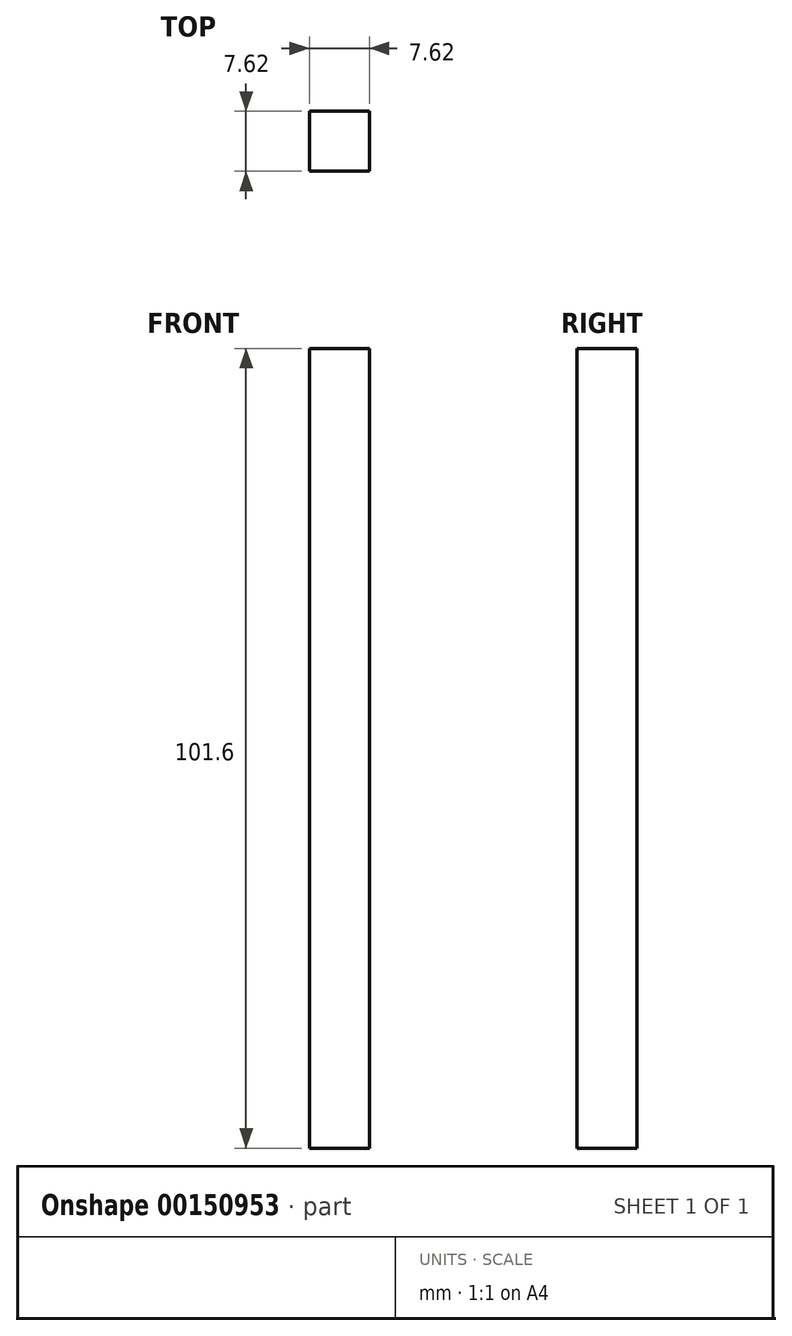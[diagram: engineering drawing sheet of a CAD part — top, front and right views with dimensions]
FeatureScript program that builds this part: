
annotation { "Feature Type Name" : "Feature", "Feature Type Description" : "" }
export const myFeature = defineFeature(function(context is Context, id is Id, definition is map)
    precondition{}
    {
        {
            var Q0;
            Q0=qCreatedBy(makeId("Front.planeOp"),FACE);
            var sketch = newSketch(context, id + "F0", { "sketchPlane" : qUnion([Q0])});
            skLineSegment(sketch, "E0.bottom", {"start": v(0, 0) * mm, "end": v(7.62, 0) * mm});
            skLineSegment(sketch, "E0.top", {"start": v(0, 101.6) * mm, "end": v(7.62, 101.6) * mm});
            skLineSegment(sketch, "E0.left", {"start": v(0, 0) * mm, "end": v(0, 101.6) * mm});
            skLineSegment(sketch, "E0.right", {"start": v(7.62, 0) * mm, "end": v(7.62, 101.6) * mm});
            skSolve(sketch);
        }
        {
            var Q0;
            Q0=makeQuery(id+"F0.imprint","IMPRINT",FACE,{"disambiguationData":[TD([[makeQuery(id+"F0.imprint","IMPRINT",EDGE,{"derivedFrom":sQuery(id+"F0.wireOp",EDGE,"E0.bottom")}),1.0]])]});
            extrude(context, id + "F1", {"entities" : qUnion([Q0]), "depth" : 7.62 * mm});
        }
    });
